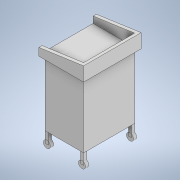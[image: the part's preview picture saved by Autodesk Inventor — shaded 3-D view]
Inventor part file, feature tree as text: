
AUTODESK INVENTOR PART (.ipt)
format: ipt  version: 2021 (Build 250183000, 183)  size: 200,704 bytes
history: native  units: mm
features: other x6, extrude x6, sketch x6, projected_geometry x4, plane x2, mirror x2
ambient origin geometry x8: Origin, YZ Plane, XZ Plane, XY Plane, X Axis, Y Axis, Z Axis, Center Point
bodies: Body1 (feature_tree), Body2 (feature_tree), Body3 (feature_tree)
feature tree (26):
  other  "實體1"
  extrude  "擠出1"  Depth=600.0mm
  extrude  "擠出2"  Depth=800.0mm
  plane  "工作平面1"
  other  "分割1"
  extrude  "擠出3"  Depth=1200.0mm TaperAngle=0.0deg
  extrude  "擠出4"  Depth=50.0mm
  extrude  "擠出5"  Depth=200.0mm TaperAngle=0.0deg
  extrude  "擠出6"  TaperAngle=0.0deg  [1 undecoded]
  mirror  "鏡射1"
  mirror  "鏡射2"
  plane  "工作平面2"
  other  "分割2"
  sketch  "草圖1"
  sketch  "草圖2"
  projected_geometry  "投影迴路1"
  sketch  "草圖3"
  projected_geometry  "投影迴路2"
  sketch  "草圖4"
  projected_geometry  "投影迴路3"
  sketch  "草圖5"
  projected_geometry  "投影迴路4"
  sketch  "草圖6"
  other  "實體2"
  other  "實體3"
  other  "實體4"
note: 1 required parameter value undecoded (feature->parameter linkage not recoverable at this tier; creation-order binding heuristic only, values carry confidence <= 0.55)
